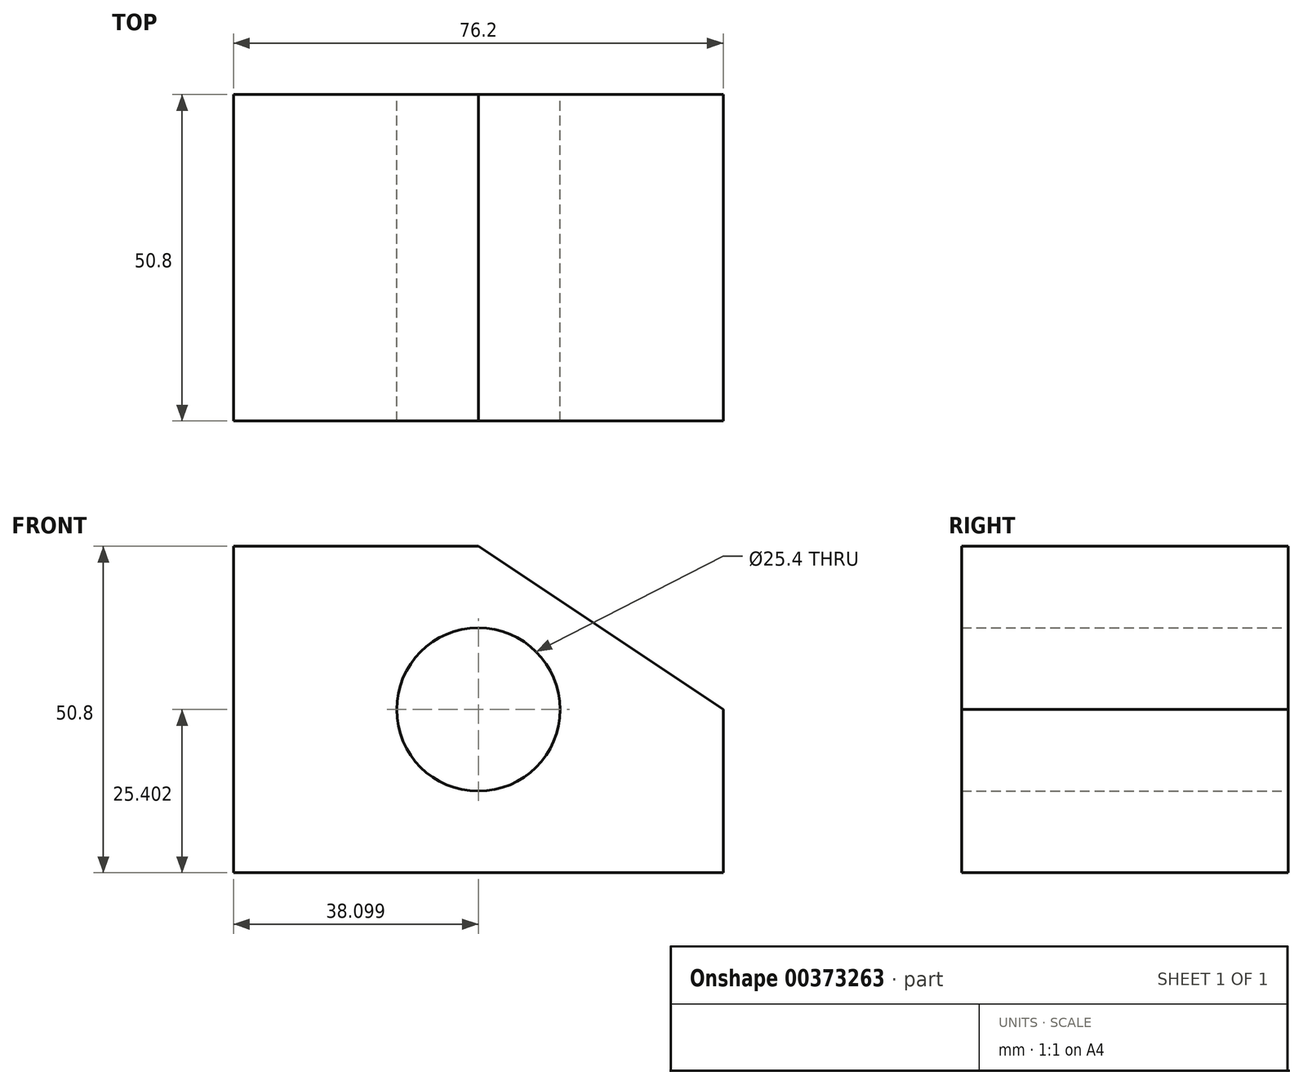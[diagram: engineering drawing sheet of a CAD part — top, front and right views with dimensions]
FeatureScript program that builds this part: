
annotation { "Feature Type Name" : "Feature", "Feature Type Description" : "" }
export const myFeature = defineFeature(function(context is Context, id is Id, definition is map)
    precondition{}
    {
        {
            var Q0;
            Q0=qCreatedBy(makeId("Front.planeOp"),FACE);
            var sketch = newSketch(context, id + "F0", { "sketchPlane" : qUnion([Q0])});
            skLineSegment(sketch, "E0", {"start": v(18.68, 20.62) * mm, "end": v(-19.42, 20.62) * mm});
            skLineSegment(sketch, "E1", {"start": v(-19.42, 20.62) * mm, "end": v(-19.42, -30.18) * mm});
            skLineSegment(sketch, "E2", {"start": v(-19.42, -30.18) * mm, "end": v(56.78, -30.18) * mm});
            skLineSegment(sketch, "E3", {"start": v(56.78, -30.18) * mm, "end": v(56.78, -4.78) * mm});
            skLineSegment(sketch, "E4", {"start": v(18.68, 20.62) * mm, "end": v(56.78, -4.78) * mm});
            skPoint(sketch, "E5", {"position": v(18.68, -4.78) * mm});
            skCircle(sketch, "E6", {"center": v(18.68, -4.78) * mm, "radius": 12.7 * mm});
            skSolve(sketch);
        }
        {
            var Q0;
            Q0=makeQuery(id+"F0.imprint","IMPRINT",FACE,{"disambiguationData":[TD([[makeQuery(id+"F0.imprint","IMPRINT",EDGE,{"derivedFrom":sQuery(id+"F0.wireOp",EDGE,"E0")}),1.0]])]});
            extrude(context, id + "F1", {"entities" : qUnion([Q0]), "endBound" : BoundingType.SYMMETRIC, "depth" : 50.8 * mm});
        }
    });
